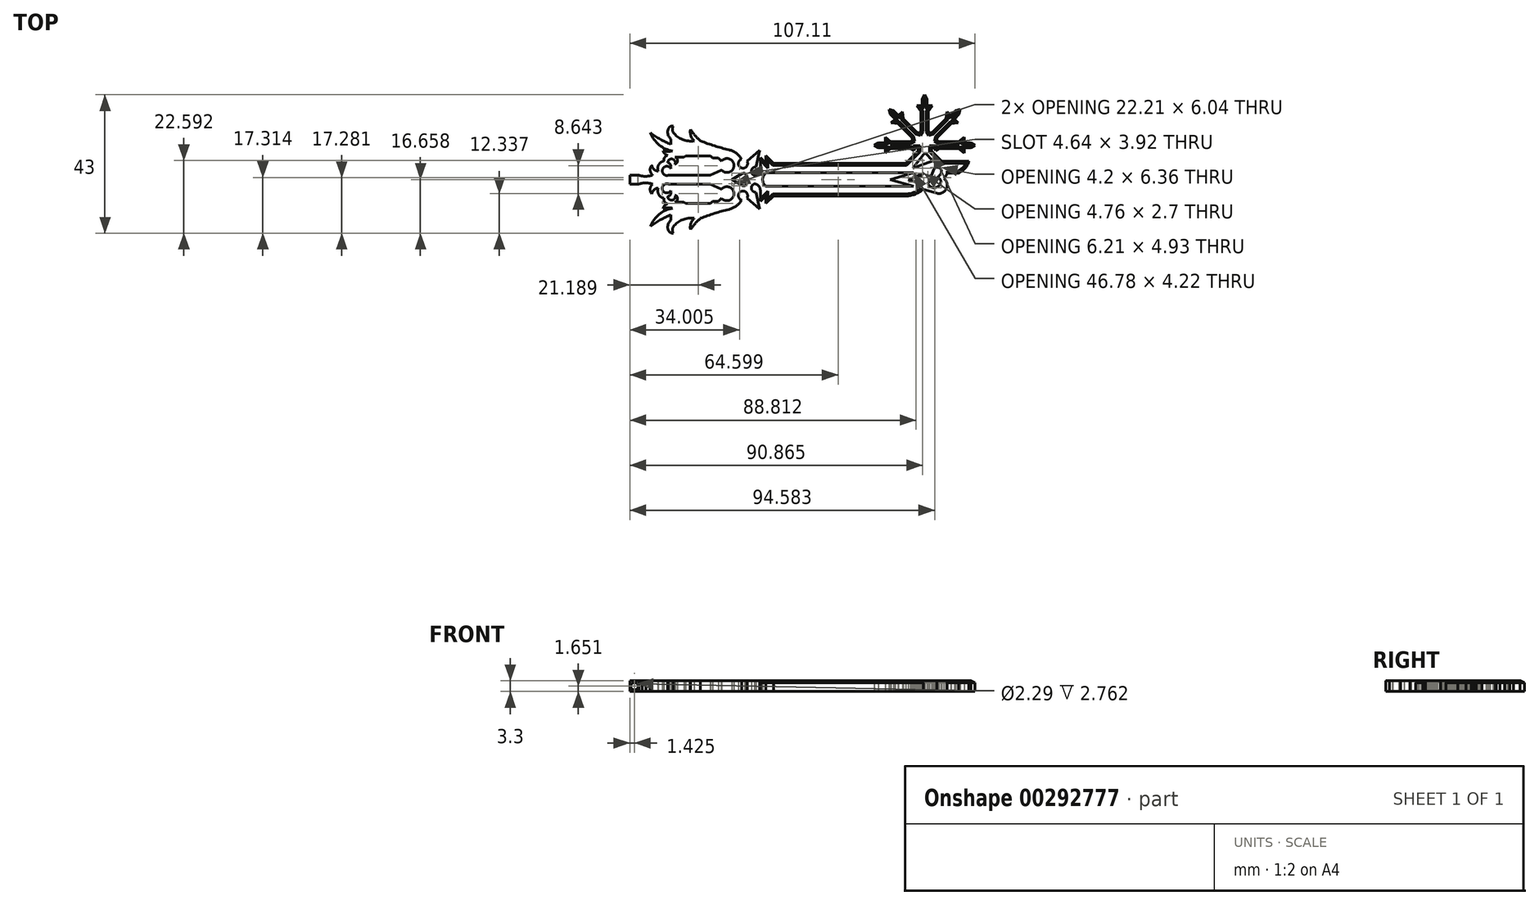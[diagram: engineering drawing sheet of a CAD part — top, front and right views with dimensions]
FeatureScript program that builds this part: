
annotation { "Feature Type Name" : "Feature", "Feature Type Description" : "" }
export const myFeature = defineFeature(function(context is Context, id is Id, definition is map)
    precondition{}
    {
        {
            var Q0;
            Q0=qCreatedBy(makeId("Top.planeOp"),FACE);
            var sketch = newSketch(context, id + "F0", { "sketchPlane" : qUnion([Q0])});
            skLineSegment(sketch, "E0", {"start": v(42.51, 19.28) * mm, "end": v(58.15, 19.28) * mm, "construction": true});
            skLineSegment(sketch, "E1", {"start": v(42.51, 19.28) * mm, "end": v(43.8, 18.52) * mm});
            skLineSegment(sketch, "E2", {"start": v(43.8, 18.52) * mm, "end": v(45.9, 18.52) * mm});
            skLineSegment(sketch, "E3", {"start": v(45.9, 18.52) * mm, "end": v(45.9, 16.83) * mm});
            skLineSegment(sketch, "E4", {"start": v(45.9, 16.83) * mm, "end": v(47.63, 18.16) * mm});
            skLineSegment(sketch, "E5", {"start": v(47.63, 18.16) * mm, "end": v(53.68, 18.16) * mm});
            skLineSegment(sketch, "E6", {"start": v(53.68, 18.16) * mm, "end": v(54.79, 17.51) * mm});
            skLineSegment(sketch, "E7", {"start": v(54.79, 17.51) * mm, "end": v(55.07, 18.46) * mm});
            skLineSegment(sketch, "E8", {"start": v(55.07, 18.46) * mm, "end": v(56.06, 18.46) * mm});
            skLineSegment(sketch, "E9.MirrorCS", {"start": v(42.51, 19.28) * mm, "end": v(43.8, 20.04) * mm});
            skLineSegment(sketch, "E10.MirrorCS", {"start": v(43.8, 20.04) * mm, "end": v(45.9, 20.04) * mm});
            skLineSegment(sketch, "E11.MirrorCS", {"start": v(45.9, 20.04) * mm, "end": v(45.9, 21.73) * mm});
            skLineSegment(sketch, "E12.MirrorCS", {"start": v(45.9, 21.73) * mm, "end": v(47.63, 20.4) * mm});
            skLineSegment(sketch, "E13.MirrorCS", {"start": v(47.63, 20.4) * mm, "end": v(53.68, 20.4) * mm});
            skLineSegment(sketch, "E14.MirrorCS", {"start": v(53.68, 20.4) * mm, "end": v(54.41, 20.83) * mm});
            skLineSegment(sketch, "E15.1.0", {"start": v(51.5, 27.51) * mm, "end": v(55.79, 23.24) * mm});
            skLineSegment(sketch, "E15.1.1", {"start": v(55.79, 23.24) * mm, "end": v(56.6, 23.02) * mm});
            skLineSegment(sketch, "E15.1.6", {"start": v(54.2, 21.65) * mm, "end": v(54.41, 20.83) * mm});
            skLineSegment(sketch, "E15.1.7", {"start": v(49.92, 25.93) * mm, "end": v(54.2, 21.65) * mm});
            skLineSegment(sketch, "E15.1.8", {"start": v(47.75, 26.2) * mm, "end": v(49.92, 25.93) * mm});
            skLineSegment(sketch, "E15.1.9", {"start": v(48.95, 27.4) * mm, "end": v(47.75, 26.2) * mm});
            skLineSegment(sketch, "E15.1.10", {"start": v(47.47, 28.89) * mm, "end": v(48.95, 27.4) * mm});
            skLineSegment(sketch, "E15.1.11", {"start": v(47.1, 30.34) * mm, "end": v(47.47, 28.89) * mm});
            skLineSegment(sketch, "E15.1.12", {"start": v(47.1, 30.34) * mm, "end": v(48.55, 29.96) * mm});
            skLineSegment(sketch, "E15.1.13", {"start": v(48.55, 29.96) * mm, "end": v(50.03, 28.48) * mm});
            skLineSegment(sketch, "E15.1.14", {"start": v(50.03, 28.48) * mm, "end": v(51.22, 29.68) * mm});
            skLineSegment(sketch, "E15.1.15", {"start": v(51.22, 29.68) * mm, "end": v(51.5, 27.51) * mm});
            skLineSegment(sketch, "E15.2.0", {"start": v(59.28, 29.8) * mm, "end": v(59.28, 23.75) * mm});
            skLineSegment(sketch, "E15.2.1", {"start": v(59.28, 23.75) * mm, "end": v(59.92, 22.65) * mm});
            skLineSegment(sketch, "E15.2.6", {"start": v(57.03, 23.75) * mm, "end": v(56.6, 23.02) * mm});
            skLineSegment(sketch, "E15.2.7", {"start": v(57.03, 29.8) * mm, "end": v(57.03, 23.75) * mm});
            skLineSegment(sketch, "E15.2.8", {"start": v(55.7, 31.53) * mm, "end": v(57.03, 29.8) * mm});
            skLineSegment(sketch, "E15.2.9", {"start": v(57.4, 31.53) * mm, "end": v(55.7, 31.53) * mm});
            skLineSegment(sketch, "E15.2.10", {"start": v(57.4, 33.63) * mm, "end": v(57.4, 31.53) * mm});
            skLineSegment(sketch, "E15.2.11", {"start": v(58.15, 34.92) * mm, "end": v(57.4, 33.63) * mm});
            skLineSegment(sketch, "E15.2.12", {"start": v(58.15, 34.92) * mm, "end": v(58.91, 33.63) * mm});
            skLineSegment(sketch, "E15.2.13", {"start": v(58.91, 33.63) * mm, "end": v(58.91, 31.53) * mm});
            skLineSegment(sketch, "E15.2.14", {"start": v(58.91, 31.53) * mm, "end": v(60.6, 31.53) * mm});
            skLineSegment(sketch, "E15.2.15", {"start": v(60.6, 31.53) * mm, "end": v(59.28, 29.8) * mm});
            skLineSegment(sketch, "E15.3.0", {"start": v(66.39, 25.93) * mm, "end": v(62.1, 21.65) * mm});
            skLineSegment(sketch, "E15.3.1", {"start": v(62.1, 21.65) * mm, "end": v(61.9, 20.83) * mm});
            skLineSegment(sketch, "E15.3.6", {"start": v(60.52, 23.24) * mm, "end": v(59.7, 23.02) * mm});
            skLineSegment(sketch, "E15.3.7", {"start": v(64.8, 27.51) * mm, "end": v(60.52, 23.24) * mm});
            skLineSegment(sketch, "E15.3.8", {"start": v(65.08, 29.68) * mm, "end": v(64.8, 27.51) * mm});
            skLineSegment(sketch, "E15.3.9", {"start": v(66.28, 28.48) * mm, "end": v(65.08, 29.68) * mm});
            skLineSegment(sketch, "E15.3.10", {"start": v(67.76, 29.96) * mm, "end": v(66.28, 28.48) * mm});
            skLineSegment(sketch, "E15.3.11", {"start": v(69.21, 30.34) * mm, "end": v(67.76, 29.96) * mm});
            skLineSegment(sketch, "E15.3.12", {"start": v(69.21, 30.34) * mm, "end": v(68.84, 28.89) * mm});
            skLineSegment(sketch, "E15.3.13", {"start": v(68.84, 28.89) * mm, "end": v(67.36, 27.4) * mm});
            skLineSegment(sketch, "E15.3.14", {"start": v(67.36, 27.4) * mm, "end": v(68.55, 26.2) * mm});
            skLineSegment(sketch, "E15.3.15", {"start": v(68.55, 26.2) * mm, "end": v(66.39, 25.93) * mm});
            skLineSegment(sketch, "E15.4.0", {"start": v(68.68, 18.16) * mm, "end": v(62.63, 18.16) * mm});
            skLineSegment(sketch, "E15.4.1", {"start": v(62.63, 18.16) * mm, "end": v(61.52, 17.51) * mm});
            skLineSegment(sketch, "E15.4.2", {"start": v(61.52, 17.51) * mm, "end": v(61.24, 18.46) * mm});
            skLineSegment(sketch, "E15.4.3", {"start": v(61.24, 18.46) * mm, "end": v(60.25, 18.46) * mm});
            skLineSegment(sketch, "E15.4.6", {"start": v(62.63, 20.4) * mm, "end": v(61.9, 20.83) * mm});
            skLineSegment(sketch, "E15.4.7", {"start": v(68.68, 20.4) * mm, "end": v(62.63, 20.4) * mm});
            skLineSegment(sketch, "E15.4.8", {"start": v(70.4, 21.73) * mm, "end": v(68.68, 20.4) * mm});
            skLineSegment(sketch, "E15.4.9", {"start": v(70.4, 20.04) * mm, "end": v(70.4, 21.73) * mm});
            skLineSegment(sketch, "E15.4.10", {"start": v(72.5, 20.04) * mm, "end": v(70.4, 20.04) * mm});
            skLineSegment(sketch, "E15.4.11", {"start": v(73.8, 19.28) * mm, "end": v(72.5, 20.04) * mm});
            skLineSegment(sketch, "E15.4.12", {"start": v(73.8, 19.28) * mm, "end": v(72.5, 18.52) * mm});
            skLineSegment(sketch, "E15.4.13", {"start": v(72.5, 18.52) * mm, "end": v(70.4, 18.52) * mm});
            skLineSegment(sketch, "E15.4.14", {"start": v(70.4, 18.52) * mm, "end": v(70.4, 16.83) * mm});
            skLineSegment(sketch, "E15.4.15", {"start": v(70.4, 16.83) * mm, "end": v(68.68, 18.16) * mm});
            skPoint(sketch, "E15.center", {"position": v(58.15, 19.28) * mm});
            skLineSegment(sketch, "E15.anchor1", {"start": v(58.15, 19.28) * mm, "end": v(47.63, 20.4) * mm, "construction": true});
            skLineSegment(sketch, "E15.anchor2", {"start": v(58.15, 19.28) * mm, "end": v(68.68, 18.16) * mm, "construction": true});
            skPoint(sketch, "E16.orphan", {"position": v(54.52, 20.41) * mm});
            skPoint(sketch, "E17.orphan", {"position": v(54.79, 21.05) * mm});
            skPoint(sketch, "E18.orphan", {"position": v(56.38, 22.65) * mm});
            skPoint(sketch, "E19.orphan", {"position": v(57.02, 22.91) * mm});
            skPoint(sketch, "E20.orphan", {"position": v(59.92, 22.65) * mm});
            skPoint(sketch, "E21.orphan", {"position": v(59.28, 22.91) * mm});
            skPoint(sketch, "E22.orphan", {"position": v(61.52, 21.05) * mm});
            skPoint(sketch, "E23.orphan", {"position": v(61.79, 20.41) * mm});
            skPoint(sketch, "E24.MirrorCS.end.orphan", {"position": v(55.07, 20.1) * mm});
            skPoint(sketch, "E25.MirrorCS.end.orphan", {"position": v(56.06, 20.1) * mm});
            skLineSegment(sketch, "E26", {"start": v(56.06, 18.46) * mm, "end": v(56.06, 17.46) * mm});
            skLineSegment(sketch, "E27", {"start": v(60.25, 18.46) * mm, "end": v(60.25, 17.46) * mm});
            skLineSegment(sketch, "E28", {"start": v(56.06, 17.46) * mm, "end": v(52.26, 13.66) * mm});
            skLineSegment(sketch, "E29", {"start": v(52.26, 13.66) * mm, "end": v(11.25, 13.66) * mm});
            skLineSegment(sketch, "E30", {"start": v(11.25, 13.66) * mm, "end": v(8.9, 16.02) * mm});
            skLineSegment(sketch, "E31", {"start": v(8.9, 16.02) * mm, "end": v(8.9, 13.66) * mm});
            skLineSegment(sketch, "E32", {"start": v(8.9, 13.66) * mm, "end": v(7.16, 15.4) * mm});
            skLineSegment(sketch, "E33", {"start": v(7.16, 15.4) * mm, "end": v(7.16, 11.84) * mm});
            skLineSegment(sketch, "E34", {"start": v(2.79, 8.58) * mm, "end": v(54.37, 8.58) * mm, "construction": true});
            skLineSegment(sketch, "E35.MirrorCS", {"start": v(7.16, 1.76) * mm, "end": v(7.16, 5.31) * mm});
            skLineSegment(sketch, "E36.MirrorCS", {"start": v(8.9, 3.5) * mm, "end": v(7.16, 1.76) * mm});
            skLineSegment(sketch, "E37.MirrorCS", {"start": v(8.9, 1.14) * mm, "end": v(8.9, 3.5) * mm});
            skLineSegment(sketch, "E38.MirrorCS", {"start": v(11.25, 3.5) * mm, "end": v(8.9, 1.14) * mm});
            skLineSegment(sketch, "E39.MirrorCS", {"start": v(52.26, 3.5) * mm, "end": v(11.25, 3.5) * mm});
            skLineSegment(sketch, "E40", {"start": v(8.9, 10.7) * mm, "end": v(54.67, 10.7) * mm});
            skLineSegment(sketch, "E41", {"start": v(54.67, 10.7) * mm, "end": v(47.52, 8.58) * mm});
            skLineSegment(sketch, "E42.MirrorCS", {"start": v(8.9, 6.47) * mm, "end": v(54.67, 6.47) * mm});
            skLineSegment(sketch, "E43.MirrorCS", {"start": v(54.67, 6.47) * mm, "end": v(47.52, 8.58) * mm});
            skArc(sketch, "E44", {"start": v(8.9, 10.7) * mm, "mid": v(7.89, 8.58) * mm, "end": v(8.9, 6.47) * mm});
            skArc(sketch, "E45", {"start": v(52.26, 3.5) * mm, "mid": v(55.17, 4.03) * mm, "end": v(57.7, 5.57) * mm});
            skLineSegment(sketch, "E46", {"start": v(54.44, 12.05) * mm, "end": v(58.22, 16.98) * mm});
            skLineSegment(sketch, "E47", {"start": v(58.22, 16.98) * mm, "end": v(60.65, 14.42) * mm});
            skLineSegment(sketch, "E48", {"start": v(60.65, 14.42) * mm, "end": v(54.44, 12.05) * mm});
            skLineSegment(sketch, "E49", {"start": v(53.11, 8.58) * mm, "end": v(57.87, 10.55) * mm});
            skLineSegment(sketch, "E50", {"start": v(57.87, 10.55) * mm, "end": v(55.4, 7.85) * mm});
            skLineSegment(sketch, "E51", {"start": v(55.4, 7.85) * mm, "end": v(53.11, 8.58) * mm});
            skLineSegment(sketch, "E52", {"start": v(57.7, 5.57) * mm, "end": v(61.9, 4.33) * mm});
            skArc(sketch, "E53", {"start": v(61.9, 4.33) * mm, "mid": v(64.9, 5.7) * mm, "end": v(64.16, 8.92) * mm});
            skArc(sketch, "E54", {"start": v(64.16, 8.92) * mm, "mid": v(64.76, 9.7) * mm, "end": v(65.1, 10.63) * mm});
            skLineSegment(sketch, "E55", {"start": v(59.16, 7.32) * mm, "end": v(61.24, 12.11) * mm});
            skArc(sketch, "E56", {"start": v(63.2, 10.44) * mm, "mid": v(62.92, 12.1) * mm, "end": v(61.24, 12.11) * mm});
            skArc(sketch, "E57", {"start": v(62.02, 9.26) * mm, "mid": v(62.68, 9.77) * mm, "end": v(63.2, 10.44) * mm});
            skArc(sketch, "E58", {"start": v(63.2, 7.93) * mm, "mid": v(62.86, 8.81) * mm, "end": v(62.02, 9.26) * mm});
            skArc(sketch, "E59", {"start": v(59.16, 7.32) * mm, "mid": v(61.42, 6.06) * mm, "end": v(63.2, 7.93) * mm});
            skLineSegment(sketch, "E60", {"start": v(60.25, 17.46) * mm, "end": v(63.46, 14.22) * mm});
            skLineSegment(sketch, "E61", {"start": v(63.46, 14.22) * mm, "end": v(71.89, 14.22) * mm});
            skArc(sketch, "E62", {"start": v(68.65, 10.63) * mm, "mid": v(70.68, 12.06) * mm, "end": v(71.89, 14.22) * mm});
            skLineSegment(sketch, "E63", {"start": v(68.65, 10.63) * mm, "end": v(65.1, 10.63) * mm});
            skArc(sketch, "E64", {"start": v(5.33, 9.92) * mm, "mid": v(6.63, 10.52) * mm, "end": v(7.16, 11.84) * mm});
            skArc(sketch, "E65", {"start": v(5.79, 12.49) * mm, "mid": v(4.4, 11.41) * mm, "end": v(5.33, 9.92) * mm});
            skLineSegment(sketch, "E66", {"start": v(5.79, 12.49) * mm, "end": v(6.93, 17.73) * mm});
            skLineSegment(sketch, "E67", {"start": v(6.93, 17.73) * mm, "end": v(3.04, 14.28) * mm});
            skArc(sketch, "E68", {"start": v(1.34, 14.93) * mm, "mid": v(1.28, 12.22) * mm, "end": v(3.04, 14.28) * mm});
            skArc(sketch, "E69", {"start": v(1.34, 14.93) * mm, "mid": v(-0.33, 16.79) * mm, "end": v(-2.6, 17.83) * mm});
            skArc(sketch, "E70", {"start": v(-11.42, 20.6) * mm, "mid": v(-7.06, 19.06) * mm, "end": v(-2.6, 17.83) * mm});
            skArc(sketch, "E71", {"start": v(-14.5, 24.14) * mm, "mid": v(-13.09, 22.26) * mm, "end": v(-11.42, 20.6) * mm});
            skArc(sketch, "E72", {"start": v(-14.5, 24.14) * mm, "mid": v(-14.41, 22.21) * mm, "end": v(-13.35, 20.6) * mm});
            skArc(sketch, "E73", {"start": v(-19.88, 23.21) * mm, "mid": v(-16.97, 21.02) * mm, "end": v(-13.35, 20.6) * mm});
            skArc(sketch, "E74", {"start": v(-19.88, 25.22) * mm, "mid": v(-20.11, 24.22) * mm, "end": v(-19.88, 23.21) * mm});
            skArc(sketch, "E75", {"start": v(-19.88, 25.22) * mm, "mid": v(-20.8, 25.03) * mm, "end": v(-21.4, 24.32) * mm});
            skArc(sketch, "E76", {"start": v(-21.4, 24.32) * mm, "mid": v(-21.5, 22.6) * mm, "end": v(-20.6, 21.14) * mm});
            skLineSegment(sketch, "E77", {"start": v(-20.6, 21.14) * mm, "end": v(-20.6, 19.52) * mm});
            skArc(sketch, "E78", {"start": v(-26.9, 23.1) * mm, "mid": v(-23.86, 21.1) * mm, "end": v(-20.6, 19.52) * mm});
            skArc(sketch, "E79", {"start": v(-26.9, 23.1) * mm, "mid": v(-24.26, 19.34) * mm, "end": v(-20.05, 17.47) * mm});
            skArc(sketch, "E80", {"start": v(-23, 17.47) * mm, "mid": v(-21.53, 17.32) * mm, "end": v(-20.05, 17.47) * mm});
            skArc(sketch, "E81", {"start": v(-23, 17.47) * mm, "mid": v(-22.47, 16.6) * mm, "end": v(-21.57, 16.1) * mm});
            skArc(sketch, "E82", {"start": v(-21.57, 16.1) * mm, "mid": v(-22.53, 15.47) * mm, "end": v(-22.76, 14.34) * mm});
            skArc(sketch, "E83", {"start": v(-22.76, 14.34) * mm, "mid": v(-24.4, 13.2) * mm, "end": v(-24.54, 11.22) * mm});
            skArc(sketch, "E84", {"start": v(-26.52, 13) * mm, "mid": v(-25.86, 11.75) * mm, "end": v(-24.54, 11.22) * mm});
            skArc(sketch, "E85", {"start": v(-26.52, 13) * mm, "mid": v(-27.04, 11.42) * mm, "end": v(-26.25, 9.96) * mm});
            skArc(sketch, "E86", {"start": v(-28.6, 9.62) * mm, "mid": v(-27.41, 9.69) * mm, "end": v(-26.25, 9.96) * mm});
            skArc(sketch, "E87", {"start": v(-19.3, 13.39) * mm, "mid": v(-20.13, 14.96) * mm, "end": v(-21.57, 13.92) * mm});
            skArc(sketch, "E88", {"start": v(-19.3, 13.39) * mm, "mid": v(-18.55, 14.47) * mm, "end": v(-19.3, 15.56) * mm});
            skArc(sketch, "E89", {"start": v(-20.6, 12.02) * mm, "mid": v(-23.2, 11.76) * mm, "end": v(-21.3, 9.96) * mm});
            skArc(sketch, "E90", {"start": v(-20.6, 12.02) * mm, "mid": v(-20.7, 13.16) * mm, "end": v(-21.57, 13.92) * mm});
            skLineSegment(sketch, "E91", {"start": v(-21.3, 9.96) * mm, "end": v(-8.42, 9.96) * mm});
            skLineSegment(sketch, "E92", {"start": v(-19.3, 15.56) * mm, "end": v(-16.5, 15.56) * mm});
            skLineSegment(sketch, "E93", {"start": v(-16.5, 15.56) * mm, "end": v(-16.04, 15.92) * mm});
            skLineSegment(sketch, "E94", {"start": v(-16.04, 15.92) * mm, "end": v(-8.27, 15.92) * mm});
            skLineSegment(sketch, "E95", {"start": v(-8.27, 15.92) * mm, "end": v(-7.68, 15.35) * mm});
            skLineSegment(sketch, "E96", {"start": v(-7.68, 15.35) * mm, "end": v(-5.9, 15.3) * mm});
            skLineSegment(sketch, "E97", {"start": v(-5.9, 15.3) * mm, "end": v(-4.92, 14.28) * mm});
            skLineSegment(sketch, "E98", {"start": v(-8.42, 9.96) * mm, "end": v(-4.98, 11.52) * mm});
            skArc(sketch, "E99", {"start": v(-4.84, 11.52) * mm, "mid": v(-1.03, 13.02) * mm, "end": v(-4.92, 14.28) * mm});
            skLineSegment(sketch, "E100", {"start": v(-1.72, 8.53) * mm, "end": v(1.52, 10.4) * mm});
            skArc(sketch, "E101", {"start": v(2.2, 8.57) * mm, "mid": v(2.95, 9.9) * mm, "end": v(1.52, 10.4) * mm});
            skArc(sketch, "E102.MirrorCS", {"start": v(5.33, 7.24) * mm, "mid": v(6.63, 6.64) * mm, "end": v(7.16, 5.31) * mm});
            skArc(sketch, "E103.MirrorCS", {"start": v(5.79, 4.67) * mm, "mid": v(4.4, 5.75) * mm, "end": v(5.33, 7.24) * mm});
            skLineSegment(sketch, "E104.MirrorCS", {"start": v(5.79, 4.67) * mm, "end": v(6.93, -0.58) * mm});
            skLineSegment(sketch, "E105.MirrorCS", {"start": v(6.93, -0.58) * mm, "end": v(3.04, 2.88) * mm});
            skArc(sketch, "E106.MirrorCS", {"start": v(1.34, 2.23) * mm, "mid": v(1.28, 4.94) * mm, "end": v(3.04, 2.88) * mm});
            skArc(sketch, "E107.MirrorCS", {"start": v(1.34, 2.23) * mm, "mid": v(-0.33, 0.37) * mm, "end": v(-2.6, -0.68) * mm});
            skArc(sketch, "E108.MirrorCS", {"start": v(-11.42, -3.45) * mm, "mid": v(-7.06, -1.9) * mm, "end": v(-2.6, -0.68) * mm});
            skArc(sketch, "E109.MirrorCS", {"start": v(-14.5, -6.98) * mm, "mid": v(-13.09, -5.1) * mm, "end": v(-11.42, -3.45) * mm});
            skArc(sketch, "E110.MirrorCS", {"start": v(-14.5, -6.98) * mm, "mid": v(-14.41, -5.06) * mm, "end": v(-13.35, -3.45) * mm});
            skArc(sketch, "E111.MirrorCS", {"start": v(-19.88, -6.06) * mm, "mid": v(-16.97, -3.86) * mm, "end": v(-13.35, -3.45) * mm});
            skArc(sketch, "E112.MirrorCS", {"start": v(-19.88, -8.06) * mm, "mid": v(-20.11, -7.06) * mm, "end": v(-19.88, -6.06) * mm});
            skArc(sketch, "E113.MirrorCS", {"start": v(-21.4, -7.16) * mm, "mid": v(-21.5, -5.45) * mm, "end": v(-20.6, -3.99) * mm});
            skLineSegment(sketch, "E114.MirrorCS", {"start": v(-20.6, -3.99) * mm, "end": v(-20.6, -2.36) * mm});
            skArc(sketch, "E115.MirrorCS", {"start": v(-26.9, -5.95) * mm, "mid": v(-23.86, -3.95) * mm, "end": v(-20.6, -2.36) * mm});
            skArc(sketch, "E116.MirrorCS", {"start": v(-26.9, -5.95) * mm, "mid": v(-24.26, -2.18) * mm, "end": v(-20.05, -0.32) * mm});
            skArc(sketch, "E117.MirrorCS", {"start": v(-23, -0.32) * mm, "mid": v(-21.53, -0.16) * mm, "end": v(-20.05, -0.32) * mm});
            skArc(sketch, "E118.MirrorCS", {"start": v(-23, -0.32) * mm, "mid": v(-22.47, 0.56) * mm, "end": v(-21.57, 1.06) * mm});
            skArc(sketch, "E119.MirrorCS", {"start": v(-21.57, 1.06) * mm, "mid": v(-22.53, 1.69) * mm, "end": v(-22.76, 2.82) * mm});
            skArc(sketch, "E120.MirrorCS", {"start": v(-22.76, 2.82) * mm, "mid": v(-24.4, 3.95) * mm, "end": v(-24.54, 5.94) * mm});
            skArc(sketch, "E121.MirrorCS", {"start": v(-26.52, 4.15) * mm, "mid": v(-25.86, 5.41) * mm, "end": v(-24.54, 5.94) * mm});
            skArc(sketch, "E122.MirrorCS", {"start": v(-26.52, 4.15) * mm, "mid": v(-27.04, 5.73) * mm, "end": v(-26.25, 7.2) * mm});
            skArc(sketch, "E123.MirrorCS", {"start": v(-30.55, 7.2) * mm, "mid": v(-30.05, 7.34) * mm, "end": v(-29.55, 7.45) * mm});
            skLineSegment(sketch, "E124.MirrorCS", {"start": v(-21.3, 7.2) * mm, "end": v(-8.42, 7.2) * mm});
            skArc(sketch, "E125.MirrorCS", {"start": v(-20.6, 5.14) * mm, "mid": v(-23.2, 5.4) * mm, "end": v(-21.3, 7.2) * mm});
            skArc(sketch, "E126.MirrorCS", {"start": v(-20.6, 5.14) * mm, "mid": v(-20.7, 4) * mm, "end": v(-21.57, 3.24) * mm});
            skArc(sketch, "E127.MirrorCS", {"start": v(-19.3, 3.77) * mm, "mid": v(-20.13, 2.2) * mm, "end": v(-21.57, 3.24) * mm});
            skArc(sketch, "E128.MirrorCS", {"start": v(-19.3, 3.77) * mm, "mid": v(-18.55, 2.68) * mm, "end": v(-19.3, 1.6) * mm});
            skLineSegment(sketch, "E129.MirrorCS", {"start": v(-19.3, 1.6) * mm, "end": v(-16.5, 1.6) * mm});
            skLineSegment(sketch, "E130.MirrorCS", {"start": v(-16.5, 1.6) * mm, "end": v(-16.04, 1.24) * mm});
            skLineSegment(sketch, "E131.MirrorCS", {"start": v(-16.04, 1.24) * mm, "end": v(-8.27, 1.24) * mm});
            skLineSegment(sketch, "E132.MirrorCS", {"start": v(-8.27, 1.24) * mm, "end": v(-7.68, 1.8) * mm});
            skLineSegment(sketch, "E133.MirrorCS", {"start": v(-7.68, 1.8) * mm, "end": v(-5.9, 1.85) * mm});
            skLineSegment(sketch, "E134.MirrorCS", {"start": v(-5.9, 1.85) * mm, "end": v(-4.92, 2.87) * mm});
            skArc(sketch, "E135.MirrorCS", {"start": v(-4.84, 5.63) * mm, "mid": v(-1.03, 4.14) * mm, "end": v(-4.92, 2.87) * mm});
            skLineSegment(sketch, "E136.MirrorCS", {"start": v(-8.42, 7.2) * mm, "end": v(-4.98, 5.63) * mm});
            skLineSegment(sketch, "E137", {"start": v(-4.84, 11.52) * mm, "end": v(-4.98, 11.52) * mm});
            skLineSegment(sketch, "E138", {"start": v(-4.84, 5.63) * mm, "end": v(-4.98, 5.63) * mm});
            skLineSegment(sketch, "E139.MirrorCS", {"start": v(-1.72, 8.63) * mm, "end": v(1.52, 6.75) * mm});
            skArc(sketch, "E140.MirrorCS", {"start": v(2.2, 8.58) * mm, "mid": v(2.95, 7.26) * mm, "end": v(1.52, 6.75) * mm});
            skPoint(sketch, "E141.orphan", {"position": v(-32.08, 8.9) * mm});
            skPoint(sketch, "E142.orphan", {"position": v(-32.08, 8.25) * mm});
            skArc(sketch, "E143.trimOffspring", {"start": v(-28.35, 7.54) * mm, "mid": v(-27.29, 7.45) * mm, "end": v(-26.25, 7.2) * mm});
            skArc(sketch, "E144.MirrorCS", {"start": v(-19.88, -8.06) * mm, "mid": v(-20.8, -7.87) * mm, "end": v(-21.4, -7.16) * mm});
            skArc(sketch, "E145", {"start": v(-30.55, 9.96) * mm, "mid": v(-29.6, 9.69) * mm, "end": v(-28.6, 9.62) * mm});
            skArc(sketch, "E146", {"start": v(-28.35, 7.54) * mm, "mid": v(-28.95, 7.53) * mm, "end": v(-29.55, 7.45) * mm});
            skPoint(sketch, "E147.center.orphan", {"position": v(-31.18, 8.25) * mm});
            skLineSegment(sketch, "E148.bottom", {"start": v(-30.55, 7.2) * mm, "end": v(-33.32, 7.2) * mm});
            skLineSegment(sketch, "E148.top", {"start": v(-30.55, 9.96) * mm, "end": v(-33.32, 9.96) * mm});
            skLineSegment(sketch, "E148.left", {"start": v(-30.55, 9.96) * mm, "end": v(-30.55, 9.96) * mm});
            skLineSegment(sketch, "E148.right", {"start": v(-33.32, 7.2) * mm, "end": v(-33.32, 9.96) * mm});
            skPoint(sketch, "E149.MirrorCS.end.orphan", {"position": v(-30.55, 7.2) * mm});
            skSolve(sketch);
        }
        {
            var Q0;
            Q0=makeQuery(id+"F0.imprint","IMPRINT",FACE,{"disambiguationData":[TD([[makeQuery(id+"F0.imprint","IMPRINT",EDGE,{"derivedFrom":sQuery(id+"F0.wireOp",EDGE,"E1")}),1.0]])]});
            extrude(context, id + "F1", {"entities" : qUnion([Q0]), "depth" : 3.3 * mm});
        }
        {
            var Q0;
            Q0=makeQuery(id+"F1.opExtrude","CAP_EDGE",EDGE,{"disambiguationData":[OSD([sQuery(id+"F0.wireOp",EDGE,"E29")])],"isStart":false});
            var Q1;
            Q1=makeQuery(id+"F1.opExtrude","CAP_EDGE",EDGE,{"disambiguationData":[OSD([sQuery(id+"F0.wireOp",EDGE,"E30")])],"isStart":false});
            var Q2;
            Q2=makeQuery(id+"F1.opExtrude","CAP_EDGE",EDGE,{"disambiguationData":[OSD([sQuery(id+"F0.wireOp",EDGE,"E31")])],"isStart":false});
            var Q3;
            Q3=makeQuery(id+"F1.opExtrude","CAP_EDGE",EDGE,{"disambiguationData":[OSD([sQuery(id+"F0.wireOp",EDGE,"E32")])],"isStart":false});
            var Q4;
            Q4=makeQuery(id+"F1.opExtrude","CAP_EDGE",EDGE,{"disambiguationData":[OSD([sQuery(id+"F0.wireOp",EDGE,"E36.MirrorCS")])],"isStart":false});
            var Q5;
            Q5=makeQuery(id+"F1.opExtrude","CAP_EDGE",EDGE,{"disambiguationData":[OSD([sQuery(id+"F0.wireOp",EDGE,"E37.MirrorCS")])],"isStart":false});
            var Q6;
            Q6=makeQuery(id+"F1.opExtrude","CAP_EDGE",EDGE,{"disambiguationData":[OSD([sQuery(id+"F0.wireOp",EDGE,"E38.MirrorCS")])],"isStart":false});
            var Q7;
            Q7=makeQuery(id+"F1.opExtrude","CAP_EDGE",EDGE,{"disambiguationData":[OSD([sQuery(id+"F0.wireOp",EDGE,"E39.MirrorCS")])],"isStart":false});
            var Q8;
            Q8=makeQuery(id+"F1.opExtrude","CAP_EDGE",EDGE,{"disambiguationData":[OSD([sQuery(id+"F0.wireOp",EDGE,"E28")])],"isStart":false});
            var Q9;
            Q9=makeQuery(id+"F1.opExtrude","CAP_EDGE",EDGE,{"disambiguationData":[OSD([sQuery(id+"F0.wireOp",EDGE,"E5")])],"isStart":false});
            var Q10;
            Q10=makeQuery(id+"F1.opExtrude","CAP_EDGE",EDGE,{"disambiguationData":[OSD([sQuery(id+"F0.wireOp",EDGE,"E6")])],"isStart":false});
            var Q11;
            Q11=makeQuery(id+"F1.opExtrude","CAP_EDGE",EDGE,{"disambiguationData":[OSD([sQuery(id+"F0.wireOp",EDGE,"E7")])],"isStart":false});
            var Q12;
            Q12=makeQuery(id+"F1.opExtrude","CAP_EDGE",EDGE,{"disambiguationData":[OSD([sQuery(id+"F0.wireOp",EDGE,"E8")])],"isStart":false});
            var Q13;
            Q13=makeQuery(id+"F1.opExtrude","CAP_EDGE",EDGE,{"disambiguationData":[OSD([sQuery(id+"F0.wireOp",EDGE,"E26")])],"isStart":false});
            var Q14;
            Q14=makeQuery(id+"F1.opExtrude","CAP_EDGE",EDGE,{"disambiguationData":[OSD([sQuery(id+"F0.wireOp",EDGE,"E4")])],"isStart":false});
            var Q15;
            Q15=makeQuery(id+"F1.opExtrude","CAP_EDGE",EDGE,{"disambiguationData":[OSD([sQuery(id+"F0.wireOp",EDGE,"E3")])],"isStart":false});
            var Q16;
            Q16=makeQuery(id+"F1.opExtrude","CAP_EDGE",EDGE,{"disambiguationData":[OSD([sQuery(id+"F0.wireOp",EDGE,"E2")])],"isStart":false});
            var Q17;
            Q17=makeQuery(id+"F1.opExtrude","CAP_EDGE",EDGE,{"disambiguationData":[OSD([sQuery(id+"F0.wireOp",EDGE,"E1")])],"isStart":false});
            var Q18;
            Q18=makeQuery(id+"F1.opExtrude","CAP_EDGE",EDGE,{"disambiguationData":[OSD([sQuery(id+"F0.wireOp",EDGE,"E9.MirrorCS")])],"isStart":false});
            var Q19;
            Q19=makeQuery(id+"F1.opExtrude","CAP_EDGE",EDGE,{"disambiguationData":[OSD([sQuery(id+"F0.wireOp",EDGE,"E10.MirrorCS")])],"isStart":false});
            var Q20;
            Q20=makeQuery(id+"F1.opExtrude","CAP_EDGE",EDGE,{"disambiguationData":[OSD([sQuery(id+"F0.wireOp",EDGE,"E11.MirrorCS")])],"isStart":false});
            var Q21;
            Q21=makeQuery(id+"F1.opExtrude","CAP_EDGE",EDGE,{"disambiguationData":[OSD([sQuery(id+"F0.wireOp",EDGE,"E12.MirrorCS")])],"isStart":false});
            var Q22;
            Q22=makeQuery(id+"F1.opExtrude","CAP_EDGE",EDGE,{"disambiguationData":[OSD([sQuery(id+"F0.wireOp",EDGE,"E13.MirrorCS")])],"isStart":false});
            var Q23;
            Q23=makeQuery(id+"F1.opExtrude","CAP_EDGE",EDGE,{"disambiguationData":[OSD([sQuery(id+"F0.wireOp",EDGE,"E14.MirrorCS")])],"isStart":false});
            var Q24;
            Q24=makeQuery(id+"F1.opExtrude","CAP_EDGE",EDGE,{"disambiguationData":[OSD([sQuery(id+"F0.wireOp",EDGE,"E15.1.6")])],"isStart":false});
            var Q25;
            Q25=makeQuery(id+"F1.opExtrude","CAP_EDGE",EDGE,{"disambiguationData":[OSD([sQuery(id+"F0.wireOp",EDGE,"E15.1.7")])],"isStart":false});
            var Q26;
            Q26=makeQuery(id+"F1.opExtrude","CAP_EDGE",EDGE,{"disambiguationData":[OSD([sQuery(id+"F0.wireOp",EDGE,"E15.1.8")])],"isStart":false});
            var Q27;
            Q27=makeQuery(id+"F1.opExtrude","CAP_EDGE",EDGE,{"disambiguationData":[OSD([sQuery(id+"F0.wireOp",EDGE,"E15.1.9")])],"isStart":false});
            var Q28;
            Q28=makeQuery(id+"F1.opExtrude","CAP_EDGE",EDGE,{"disambiguationData":[OSD([sQuery(id+"F0.wireOp",EDGE,"E15.1.10")])],"isStart":false});
            var Q29;
            Q29=makeQuery(id+"F1.opExtrude","CAP_EDGE",EDGE,{"disambiguationData":[OSD([sQuery(id+"F0.wireOp",EDGE,"E15.1.11")])],"isStart":false});
            var Q30;
            Q30=makeQuery(id+"F1.opExtrude","CAP_EDGE",EDGE,{"disambiguationData":[OSD([sQuery(id+"F0.wireOp",EDGE,"E15.1.12")])],"isStart":false});
            var Q31;
            Q31=makeQuery(id+"F1.opExtrude","CAP_EDGE",EDGE,{"disambiguationData":[OSD([sQuery(id+"F0.wireOp",EDGE,"E15.1.13")])],"isStart":false});
            var Q32;
            Q32=makeQuery(id+"F1.opExtrude","CAP_EDGE",EDGE,{"disambiguationData":[OSD([sQuery(id+"F0.wireOp",EDGE,"E15.1.14")])],"isStart":false});
            var Q33;
            Q33=makeQuery(id+"F1.opExtrude","CAP_EDGE",EDGE,{"disambiguationData":[OSD([sQuery(id+"F0.wireOp",EDGE,"E15.1.15")])],"isStart":false});
            var Q34;
            Q34=makeQuery(id+"F1.opExtrude","CAP_EDGE",EDGE,{"disambiguationData":[OSD([sQuery(id+"F0.wireOp",EDGE,"E15.1.0")])],"isStart":false});
            var Q35;
            Q35=makeQuery(id+"F1.opExtrude","CAP_EDGE",EDGE,{"disambiguationData":[OSD([sQuery(id+"F0.wireOp",EDGE,"E15.1.1")])],"isStart":false});
            var Q36;
            Q36=makeQuery(id+"F1.opExtrude","CAP_EDGE",EDGE,{"disambiguationData":[OSD([sQuery(id+"F0.wireOp",EDGE,"E15.2.6")])],"isStart":false});
            var Q37;
            Q37=makeQuery(id+"F1.opExtrude","CAP_EDGE",EDGE,{"disambiguationData":[OSD([sQuery(id+"F0.wireOp",EDGE,"E15.2.7")])],"isStart":false});
            var Q38;
            Q38=makeQuery(id+"F1.opExtrude","CAP_EDGE",EDGE,{"disambiguationData":[OSD([sQuery(id+"F0.wireOp",EDGE,"E15.2.8")])],"isStart":false});
            var Q39;
            Q39=makeQuery(id+"F1.opExtrude","CAP_EDGE",EDGE,{"disambiguationData":[OSD([sQuery(id+"F0.wireOp",EDGE,"E15.2.9")])],"isStart":false});
            var Q40;
            Q40=makeQuery(id+"F1.opExtrude","CAP_EDGE",EDGE,{"disambiguationData":[OSD([sQuery(id+"F0.wireOp",EDGE,"E15.2.10")])],"isStart":false});
            var Q41;
            Q41=makeQuery(id+"F1.opExtrude","CAP_EDGE",EDGE,{"disambiguationData":[OSD([sQuery(id+"F0.wireOp",EDGE,"E15.2.11")])],"isStart":false});
            var Q42;
            Q42=makeQuery(id+"F1.opExtrude","CAP_EDGE",EDGE,{"disambiguationData":[OSD([sQuery(id+"F0.wireOp",EDGE,"E15.2.12")])],"isStart":false});
            var Q43;
            Q43=makeQuery(id+"F1.opExtrude","CAP_EDGE",EDGE,{"disambiguationData":[OSD([sQuery(id+"F0.wireOp",EDGE,"E15.2.13")])],"isStart":false});
            var Q44;
            Q44=makeQuery(id+"F1.opExtrude","CAP_EDGE",EDGE,{"disambiguationData":[OSD([sQuery(id+"F0.wireOp",EDGE,"E15.2.14")])],"isStart":false});
            var Q45;
            Q45=makeQuery(id+"F1.opExtrude","CAP_EDGE",EDGE,{"disambiguationData":[OSD([sQuery(id+"F0.wireOp",EDGE,"E15.2.15")])],"isStart":false});
            var Q46;
            Q46=makeQuery(id+"F1.opExtrude","CAP_EDGE",EDGE,{"disambiguationData":[OSD([sQuery(id+"F0.wireOp",EDGE,"E15.2.0")])],"isStart":false});
            var Q47;
            Q47=makeQuery(id+"F1.opExtrude","CAP_EDGE",EDGE,{"disambiguationData":[OSD([sQuery(id+"F0.wireOp",EDGE,"E15.2.1")])],"isStart":false});
            var Q48;
            Q48=makeQuery(id+"F1.opExtrude","CAP_EDGE",EDGE,{"disambiguationData":[OSD([sQuery(id+"F0.wireOp",EDGE,"E15.3.6")])],"isStart":false});
            var Q49;
            Q49=makeQuery(id+"F1.opExtrude","CAP_EDGE",EDGE,{"disambiguationData":[OSD([sQuery(id+"F0.wireOp",EDGE,"E15.3.7")])],"isStart":false});
            var Q50;
            Q50=makeQuery(id+"F1.opExtrude","CAP_EDGE",EDGE,{"disambiguationData":[OSD([sQuery(id+"F0.wireOp",EDGE,"E15.3.8")])],"isStart":false});
            var Q51;
            Q51=makeQuery(id+"F1.opExtrude","CAP_EDGE",EDGE,{"disambiguationData":[OSD([sQuery(id+"F0.wireOp",EDGE,"E15.3.9")])],"isStart":false});
            var Q52;
            Q52=makeQuery(id+"F1.opExtrude","CAP_EDGE",EDGE,{"disambiguationData":[OSD([sQuery(id+"F0.wireOp",EDGE,"E15.3.10")])],"isStart":false});
            var Q53;
            Q53=makeQuery(id+"F1.opExtrude","CAP_EDGE",EDGE,{"disambiguationData":[OSD([sQuery(id+"F0.wireOp",EDGE,"E15.3.11")])],"isStart":false});
            var Q54;
            Q54=makeQuery(id+"F1.opExtrude","CAP_EDGE",EDGE,{"disambiguationData":[OSD([sQuery(id+"F0.wireOp",EDGE,"E15.3.12")])],"isStart":false});
            var Q55;
            Q55=makeQuery(id+"F1.opExtrude","CAP_EDGE",EDGE,{"disambiguationData":[OSD([sQuery(id+"F0.wireOp",EDGE,"E15.3.13")])],"isStart":false});
            var Q56;
            Q56=makeQuery(id+"F1.opExtrude","CAP_EDGE",EDGE,{"disambiguationData":[OSD([sQuery(id+"F0.wireOp",EDGE,"E15.3.14")])],"isStart":false});
            var Q57;
            Q57=makeQuery(id+"F1.opExtrude","CAP_EDGE",EDGE,{"disambiguationData":[OSD([sQuery(id+"F0.wireOp",EDGE,"E15.3.15")])],"isStart":false});
            var Q58;
            Q58=makeQuery(id+"F1.opExtrude","CAP_EDGE",EDGE,{"disambiguationData":[OSD([sQuery(id+"F0.wireOp",EDGE,"E15.3.0")])],"isStart":false});
            var Q59;
            Q59=makeQuery(id+"F1.opExtrude","CAP_EDGE",EDGE,{"disambiguationData":[OSD([sQuery(id+"F0.wireOp",EDGE,"E15.3.1")])],"isStart":false});
            var Q60;
            Q60=makeQuery(id+"F1.opExtrude","CAP_EDGE",EDGE,{"disambiguationData":[OSD([sQuery(id+"F0.wireOp",EDGE,"E15.4.6")])],"isStart":false});
            var Q61;
            Q61=makeQuery(id+"F1.opExtrude","CAP_EDGE",EDGE,{"disambiguationData":[OSD([sQuery(id+"F0.wireOp",EDGE,"E15.4.7")])],"isStart":false});
            var Q62;
            Q62=makeQuery(id+"F1.opExtrude","CAP_EDGE",EDGE,{"disambiguationData":[OSD([sQuery(id+"F0.wireOp",EDGE,"E15.4.8")])],"isStart":false});
            var Q63;
            Q63=makeQuery(id+"F1.opExtrude","CAP_EDGE",EDGE,{"disambiguationData":[OSD([sQuery(id+"F0.wireOp",EDGE,"E15.4.9")])],"isStart":false});
            var Q64;
            Q64=makeQuery(id+"F1.opExtrude","CAP_EDGE",EDGE,{"disambiguationData":[OSD([sQuery(id+"F0.wireOp",EDGE,"E15.4.10")])],"isStart":false});
            var Q65;
            Q65=makeQuery(id+"F1.opExtrude","CAP_EDGE",EDGE,{"disambiguationData":[OSD([sQuery(id+"F0.wireOp",EDGE,"E15.4.11")])],"isStart":false});
            var Q66;
            Q66=makeQuery(id+"F1.opExtrude","CAP_EDGE",EDGE,{"disambiguationData":[OSD([sQuery(id+"F0.wireOp",EDGE,"E15.4.12")])],"isStart":false});
            var Q67;
            Q67=makeQuery(id+"F1.opExtrude","CAP_EDGE",EDGE,{"disambiguationData":[OSD([sQuery(id+"F0.wireOp",EDGE,"E15.4.13")])],"isStart":false});
            var Q68;
            Q68=makeQuery(id+"F1.opExtrude","CAP_EDGE",EDGE,{"disambiguationData":[OSD([sQuery(id+"F0.wireOp",EDGE,"E15.4.14")])],"isStart":false});
            var Q69;
            Q69=makeQuery(id+"F1.opExtrude","CAP_EDGE",EDGE,{"disambiguationData":[OSD([sQuery(id+"F0.wireOp",EDGE,"E15.4.15")])],"isStart":false});
            var Q70;
            Q70=makeQuery(id+"F1.opExtrude","CAP_EDGE",EDGE,{"disambiguationData":[OSD([sQuery(id+"F0.wireOp",EDGE,"E15.4.0")])],"isStart":false});
            var Q71;
            Q71=makeQuery(id+"F1.opExtrude","CAP_EDGE",EDGE,{"disambiguationData":[OSD([sQuery(id+"F0.wireOp",EDGE,"E15.4.1")])],"isStart":false});
            var Q72;
            Q72=makeQuery(id+"F1.opExtrude","CAP_EDGE",EDGE,{"disambiguationData":[OSD([sQuery(id+"F0.wireOp",EDGE,"E15.4.2")])],"isStart":false});
            var Q73;
            Q73=makeQuery(id+"F1.opExtrude","CAP_EDGE",EDGE,{"disambiguationData":[OSD([sQuery(id+"F0.wireOp",EDGE,"E15.4.3")])],"isStart":false});
            var Q74;
            Q74=makeQuery(id+"F1.opExtrude","CAP_EDGE",EDGE,{"disambiguationData":[OSD([sQuery(id+"F0.wireOp",EDGE,"E27")])],"isStart":false});
            var Q75;
            Q75=makeQuery(id+"F1.opExtrude","CAP_EDGE",EDGE,{"disambiguationData":[OSD([sQuery(id+"F0.wireOp",EDGE,"E60")])],"isStart":false});
            var Q76;
            Q76=makeQuery(id+"F1.opExtrude","CAP_EDGE",EDGE,{"disambiguationData":[OSD([sQuery(id+"F0.wireOp",EDGE,"E61")])],"isStart":false});
            var Q77;
            Q77=makeQuery(id+"F1.opExtrude","CAP_EDGE",EDGE,{"disambiguationData":[OSD([sQuery(id+"F0.wireOp",EDGE,"E62")])],"isStart":false});
            var Q78;
            Q78=makeQuery(id+"F1.opExtrude","CAP_EDGE",EDGE,{"disambiguationData":[OSD([sQuery(id+"F0.wireOp",EDGE,"E63")])],"isStart":false});
            var Q79;
            Q79=makeQuery(id+"F1.opExtrude","CAP_EDGE",EDGE,{"disambiguationData":[OSD([sQuery(id+"F0.wireOp",EDGE,"E45")])],"isStart":false});
            chamfer(context, id + "F2", {"entities" : qUnion([Q0, Q1, Q2, Q3, Q4, Q5, Q6, Q7, Q8, Q9, Q10, Q11, Q12, Q13, Q14, Q15, Q16, Q17, Q18, Q19, Q20, Q21, Q22, Q23, Q24, Q25, Q26, Q27, Q28, Q29, Q30, Q31, Q32, Q33, Q34, Q35, Q36, Q37, Q38, Q39, Q40, Q41, Q42, Q43, Q44, Q45, Q46, Q47, Q48, Q49, Q50, Q51, Q52, Q53, Q54, Q55, Q56, Q57, Q58, Q59, Q60, Q61, Q62, Q63, Q64, Q65, Q66, Q67, Q68, Q69, Q70, Q71, Q72, Q73, Q74, Q75, Q76, Q77, Q78, Q79]), "width" : 0.64 * mm, "tangentPropagation" : true});
        }
        {
            var Q0;
            Q0=makeQuery(id+"F1.opExtrude","SWEPT_FACE",FACE,{"disambiguationData":[OSD([sQuery(id+"F0.wireOp",EDGE,"E148.top")])]});
            var sketch = newSketch(context, id + "F3", { "sketchPlane" : qUnion([Q0])});
            skCircle(sketch, "E150", {"center": v(31.9, 1.65) * mm, "radius": 1.14 * mm});
            skSolve(sketch);
        }
        {
            var Q0;
            Q0 = qSketchRegion(id + "F3", true);
            extrude(context, id + "F4", {"entities" : qUnion([Q0]), "operationType" : NewBodyOperationType.REMOVE, "oppositeDirection" : true, "depth" : 25.4 * mm, "offsetDistance" : 25.4 * mm});
        }
    });
